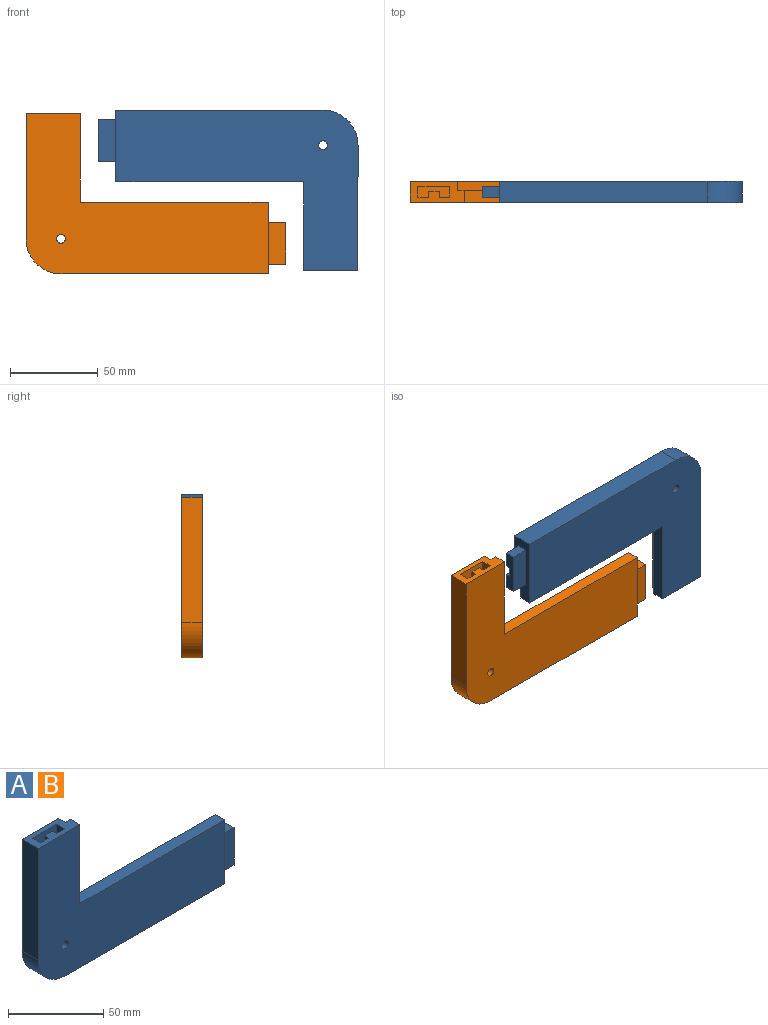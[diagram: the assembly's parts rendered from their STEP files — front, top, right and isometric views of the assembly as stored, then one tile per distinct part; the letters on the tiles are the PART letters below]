
ASSEMBLY  parts=2 mates=2
PART A: 36 faces, bbox 148.3x12x91.7 mm
  f0: plane 138.33x91.67mm, normal (0,1,0), area 4766.2mm2, adj f1,f2,f5,f6,f7,f8,f10,f11
  f1: plane 31x12mm, normal (0,0,1), area 262mm2, adj f0,f4,f5,f9,f11,f12,f22,f23
  f2: plane 41x12mm, normal (1,0,0), area 336mm2, adj f0,f3,f7,f9,f10,f12,f13,f14
  f3: plane 107.33x7mm, normal (0,0,1), area 751.3mm2, adj f2,f4,f9,f12
  f4: plane 50.67x7mm, normal (1,0,0), area 354.7mm2, adj f1,f3,f9,f12
  f5: plane 71.67x12mm, normal (-1,0,0), area 860mm2, adj f0,f1,f6,f9
  f6: cylinder r=20mm len=20mm, axis (0,1,0), area 377mm2, adj f0,f5,f7,f9
  f7: plane 118.33x12mm, normal (0,0,-1), area 1420mm2, adj f0,f2,f6,f9
  f8: cylinder r=2.5mm len=12mm, axis (0,1,0), area 188.5mm2, adj f0,f9
  f9: plane 138.33x91.67mm, normal (0,-1,0), area 7136.8mm2, adj f1,f2,f3,f4,f5,f6,f7,f8
  f10: plane 111.33x5mm, normal (0,0,1), area 556.6mm2, adj f0,f2,f11,f12
  f11: plane 56.67x5mm, normal (1,0,0), area 283.3mm2, adj f0,f1,f10,f12
  f12: plane 111.33x56.67mm, normal (0,1,0), area 870.7mm2, adj f1,f2,f3,f4,f10,f11
  f13: plane 10x6mm, normal (0,0,1), area 60mm2, adj f2,f14,f20,f21
  f14: plane 24x10mm, normal (0,-1,0), area 240mm2, adj f2,f13,f15,f21
  f15: plane 10x6mm, normal (0,0,-1), area 60mm2, adj f2,f14,f16,f21
  f16: plane 10x9mm, normal (0,1,0), area 90mm2, adj f2,f15,f17,f21
  f17: plane 10x3mm, normal (0,0,1), area 30mm2, adj f2,f16,f18,f21
  f18: plane 10x6mm, normal (0,1,0), area 60mm2, adj f2,f17,f19,f21
  f19: plane 10x3mm, normal (0,0,-1), area 30mm2, adj f2,f18,f20,f21
  f20: plane 10x9mm, normal (0,1,0), area 90mm2, adj f2,f13,f19,f21
  f21: plane 24x6mm, normal (1,0,0), area 126mm2, adj f13,f14,f15,f16,f17,f18,f19,f20
  f22: plane 25x5.79mm, normal (0,1,0), area 144.7mm2, adj f1,f23,f29,f30
  f23: plane 25x6mm, normal (-1,0,0), area 150mm2, adj f1,f22,f24,f30
  f24: plane 25x18mm, normal (0,-1,0), area 450mm2, adj f1,f23,f25,f30
  f25: plane 25x6mm, normal (1,0,0), area 150mm2, adj f1,f24,f26,f30
  f26: plane 25x6.21mm, normal (0,1,0), area 155.3mm2, adj f1,f25,f27,f30
  f27: plane 25x3mm, normal (-1,0,0), area 75mm2, adj f1,f26,f28,f30
  f28: plane 25x6mm, normal (0,1,0), area 150mm2, adj f1,f27,f29,f30
  f29: plane 25x3mm, normal (1,0,0), area 75mm2, adj f1,f22,f28,f30
  f30: plane 18x6mm, normal (0,0,1), area 90mm2, adj f22,f23,f24,f25,f26,f27,f28,f29
  f31: plane 100x8mm, normal (0,0,-1), area 800mm2, adj f0,f32,f34,f35
  f32: plane 15x8mm, normal (-1,0,0), area 120mm2, adj f0,f31,f33,f35
  f33: plane 100x8mm, normal (0,0,1), area 800mm2, adj f0,f32,f34,f35
  f34: plane 15x8mm, normal (1,0,0), area 120mm2, adj f0,f31,f33,f35
  f35: plane 100x15mm, normal (0,1,0), area 1500mm2, adj f31,f32,f33,f34
PART B: same geometry as A
PLACE A rot(axis=(0,-1,0),180deg) t=(-161.99,15.6,-104.78)mm
PLACE B t=(-106.65,15.6,-135.71)mm
MATE parallel B.f3 <-> A.f3  axis (0,0,1) through (-144.52,7.1,-126.06)mm
MATE planar A.f9 <-> B.f9  axis (0,-1,0) through (-124.13,3.6,-114.43)mm
